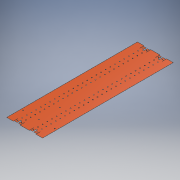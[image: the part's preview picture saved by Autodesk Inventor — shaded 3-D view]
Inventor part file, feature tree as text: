
AUTODESK INVENTOR PART (.ipt)
format: ipt  version: 2019 (Build 230136000, 136)  size: 399,872 bytes
history: native  units: mm
features: mirror x5, extrude x4, other x4
ambient origin geometry x8: Origin, YZ Plane, XZ Plane, XY Plane, X Axis, Y Axis, Z Axis, Center Point
bodies: Solid1 (feature_tree)
feature tree (13):
  extrude  "Skin Body"  Depth=1829.0mm
  extrude  "Feature Cut"  Depth=914.5mm
  mirror  "Feature Cut Side Mirror"
  mirror  "Feature Cut Mirror"
  extrude  "End Cut"  Depth=424.0mm
  mirror  "End Cut Mirror"
  extrude  "Slot Cut"  Depth=212.0mm
  mirror  "Slot Cut Side Mirror"
  mirror  "Slot Cut Mirror"
  other  "Skin Scheme"
  other  "Feature Cut Outline"
  other  "End Cut Outline"
  other  "Slot Cut Outline"
